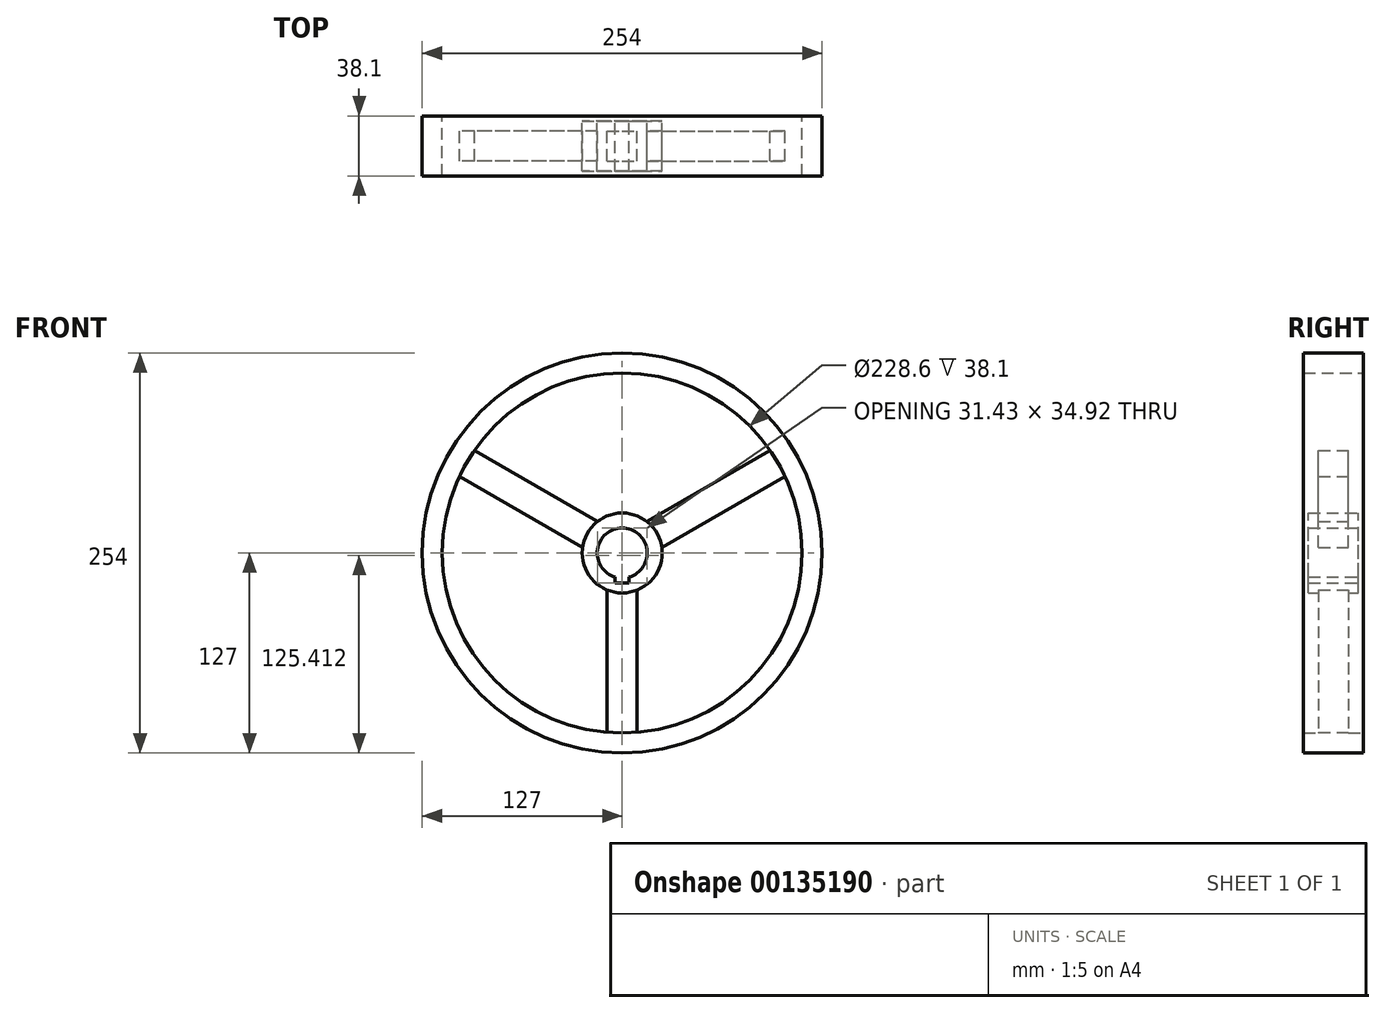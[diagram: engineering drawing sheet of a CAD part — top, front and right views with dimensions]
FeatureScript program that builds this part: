
annotation { "Feature Type Name" : "Feature", "Feature Type Description" : "" }
export const myFeature = defineFeature(function(context is Context, id is Id, definition is map)
    precondition{}
    {
        {
            var Q0;
            Q0=qCreatedBy(makeId("Front.planeOp"),FACE);
            var sketch = newSketch(context, id + "F0", { "sketchPlane" : qUnion([Q0])});
            skArc(sketch, "E0", {"start": v(4.45, -15.24) * mm, "mid": v(0, 15.88) * mm, "end": v(-4.45, -15.24) * mm});
            skCircle(sketch, "E1", {"center": v(0, 0) * mm, "radius": 25.4 * mm});
            skCircle(sketch, "E2", {"center": v(0, 0) * mm, "radius": 114.3 * mm});
            skCircle(sketch, "E3", {"center": v(0, 0) * mm, "radius": 127 * mm});
            skPoint(sketch, "E4", {"position": v(0, -19.05) * mm});
            skLineSegment(sketch, "E5", {"start": v(-4.45, -19.05) * mm, "end": v(4.45, -19.05) * mm});
            skLineSegment(sketch, "E6", {"start": v(-4.45, -19.05) * mm, "end": v(-4.45, -15.24) * mm});
            skLineSegment(sketch, "E7", {"start": v(4.45, -19.05) * mm, "end": v(4.45, -15.24) * mm});
            skLineSegment(sketch, "E8", {"start": v(0, 0) * mm, "end": v(0, -114.3) * mm, "construction": true});
            skLineSegment(sketch, "E9", {"start": v(-9.53, -23.55) * mm, "end": v(-9.52, -113.9) * mm});
            skLineSegment(sketch, "E10.MirrorCS", {"start": v(9.53, -23.55) * mm, "end": v(9.52, -113.9) * mm});
            skLineSegment(sketch, "E11.1.0", {"start": v(25.15, 3.52) * mm, "end": v(103.4, 48.7) * mm});
            skLineSegment(sketch, "E11.1.1", {"start": v(15.63, 20.02) * mm, "end": v(93.88, 65.2) * mm});
            skLineSegment(sketch, "E11.2.0", {"start": v(-15.63, 20.02) * mm, "end": v(-93.88, 65.2) * mm});
            skLineSegment(sketch, "E11.2.1", {"start": v(-25.15, 3.52) * mm, "end": v(-103.4, 48.7) * mm});
            skSolve(sketch);
        }
        {
            var Q0;
            {var subQ0=sQuery(id+"F0.wireOp",EDGE,"E11.2.0");Q0=makeQuery(id+"F0.imprint","IMPRINT",FACE,{"disambiguationData":[TD([[makeQuery(id+"F0.imprint","IMPRINT",EDGE,{"derivedFrom":subQ0}),1.0]])]});}
            var Q1;
            {var subQ0=sQuery(id+"F0.wireOp",EDGE,"E11.1.0");Q1=makeQuery(id+"F0.imprint","IMPRINT",FACE,{"disambiguationData":[TD([[makeQuery(id+"F0.imprint","IMPRINT",EDGE,{"derivedFrom":subQ0}),1.0]])]});}
            var Q2;
            {var subQ0=sQuery(id+"F0.wireOp",EDGE,"E9");Q2=makeQuery(id+"F0.imprint","IMPRINT",FACE,{"disambiguationData":[TD([[makeQuery(id+"F0.imprint","IMPRINT",EDGE,{"derivedFrom":subQ0}),1.0]])]});}
            extrude(context, id + "F1", {"entities" : qUnion([Q0, Q1, Q2]), "endBound" : BoundingType.SYMMETRIC, "depth" : 19.05 * mm});
        }
        {
            var Q0;
            Q0=makeQuery(id+"F0.imprint","IMPRINT",FACE,{"disambiguationData":[TD([[makeQuery(id+"F0.imprint","IMPRINT",EDGE,{"derivedFrom":sQuery(id+"F0.wireOp",EDGE,"E3")}),1.0]])]});
            extrude(context, id + "F2", {"entities" : qUnion([Q0]), "operationType" : NewBodyOperationType.ADD, "endBound" : BoundingType.SYMMETRIC, "depth" : 38.1 * mm});
        }
        {
            var Q0;
            Q0=makeQuery(id+"F0.imprint","IMPRINT",FACE,{"disambiguationData":[TD([[makeQuery(id+"F0.imprint","IMPRINT",EDGE,{"derivedFrom":sQuery(id+"F0.wireOp",EDGE,"E0")}),-1.0]])]});
            extrude(context, id + "F3", {"entities" : qUnion([Q0]), "operationType" : NewBodyOperationType.ADD, "endBound" : BoundingType.SYMMETRIC, "depth" : 31.75 * mm});
        }
    });
